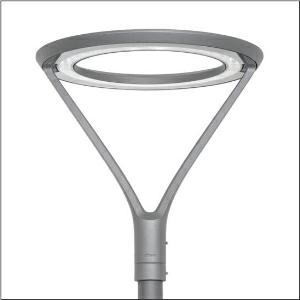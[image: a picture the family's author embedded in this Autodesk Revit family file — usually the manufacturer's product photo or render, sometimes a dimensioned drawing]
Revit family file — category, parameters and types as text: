
# Revit family: dl_r__20___pl1_2s_5xa51283ns008p_0781
name_source: partatom
category: Lighting Fixtures
units: mm (PartAtom-declared; Revit-internal decimal feet)

## family parameters
Cut with Voids When Loaded = No
Host = Face
Light Source = No
Part Type = Normal
Room Calculation Point = No
Round Connector Dimension = Use Diameter
Shared = No

## types (1)
- --- (1 x LED, 5400 lm, 41.9 W, 4000K)
    Apparent Load = 42 VA
    CIE Flux Codes = 33 78 99 100 100
    Color Rendering = 70
    Color Temperature = 4000K
    Default Elevation = 1800 mm
    Description = DL® 20, mast luminaire, primary light control with reflector, highly specular, primary optical cover: cover, of toughened safety glass of clear glass with excellent transmission level, light distribution: PL1.2s, light emission: direct distribution, primary light characteristic: symmetric, installation type: post-top, LED, High Power LED, rated luminous flux: 5.340lm, luminous efficacy: 101lm/W, light colour: 740, colour temperature: 4000K, control gear: ECG Plus, control: overheat protection, power reduction, digital communication interface, constant luminous flux control, time-dependent luminous flux control, flexible luminous flux parameterisation, electronic power reduction, mains connection: 230..240V, 50/60Hz, connection cable pre-assembled, cable length: 5m, start of lifetime: 53W, end of service life: 54W, reduction: 24W, luminaire housing, upper part, of cast aluminium, powder-coated, Siteco® metallic grey (DB 702S), diameter: 690mm, height: 690mm, spigot size: 76mm (post-top), luminaire housing, of cast aluminium, powder-coated, Siteco® metallic grey (DB 702S), equipment: Power, protection rating (complete): IP66, insulation class (complete): insulation class II (safety insulation), certification: CE, ENEC, VDE, impact resistance: IK08, permissible operating ambient temperature: -25..+30°C, standard-compliant lighting for roads and squares, packaging unit: 1 piece

Light Distribution: PL1.2s
    Height = 690 mm
    Lamp = 1 x LED
    Lamp Light Flux = 5400 lm
    Lamp Power = 41.9 W
    Lamp count = 1
    Length = 690 mm
    Luminous efficacy = 129 lm/W
    Manufacturer = Siteco
    ModVariant = No
    Model = 5XA51283NS008P
    Number of Poles = 1
    OnlyDefault = Yes
    Power Factor = 1
    Product Name = DL® 20 | PL1.2s
    Product group = mast luminaire | pylon top
    ProductGroupID = 6100
    Protection Class = Protection class II
    Protection Degree = IP 66
    RLX_Detail_Level = 1
    RLX_Emergency_Light_Flux = 0 lm
    RLX_Emergency_Type = 0
    RLX_Emergency_Type_DB = No
    RlxData = <blob elided: 204761 chars, md5=012e6d2b>
    Socket = socket
    Standby Power = 0 W
    System Light Flux = 5400 lm
    System Power = 42 W
    Type Comments = factory setting: luminous flux: 100 % | dim-lin: 254 | 565 mA
    Type Image = l_1006001.jpg
    URL = http://relux.com
    VarID = @adj_027943
    Voltage = 0 V
    Weight = 0.00 kg
    Width = 0 mm  [stored 0 ft]

note: [stored X ft] marks values corroborated as IEEE doubles in the binary element streams (Revit-internal decimal feet)

## geometry (parser evidence)
native form markers: Blend x4, Sweep x10
no freeform markers — native parametric forms only
